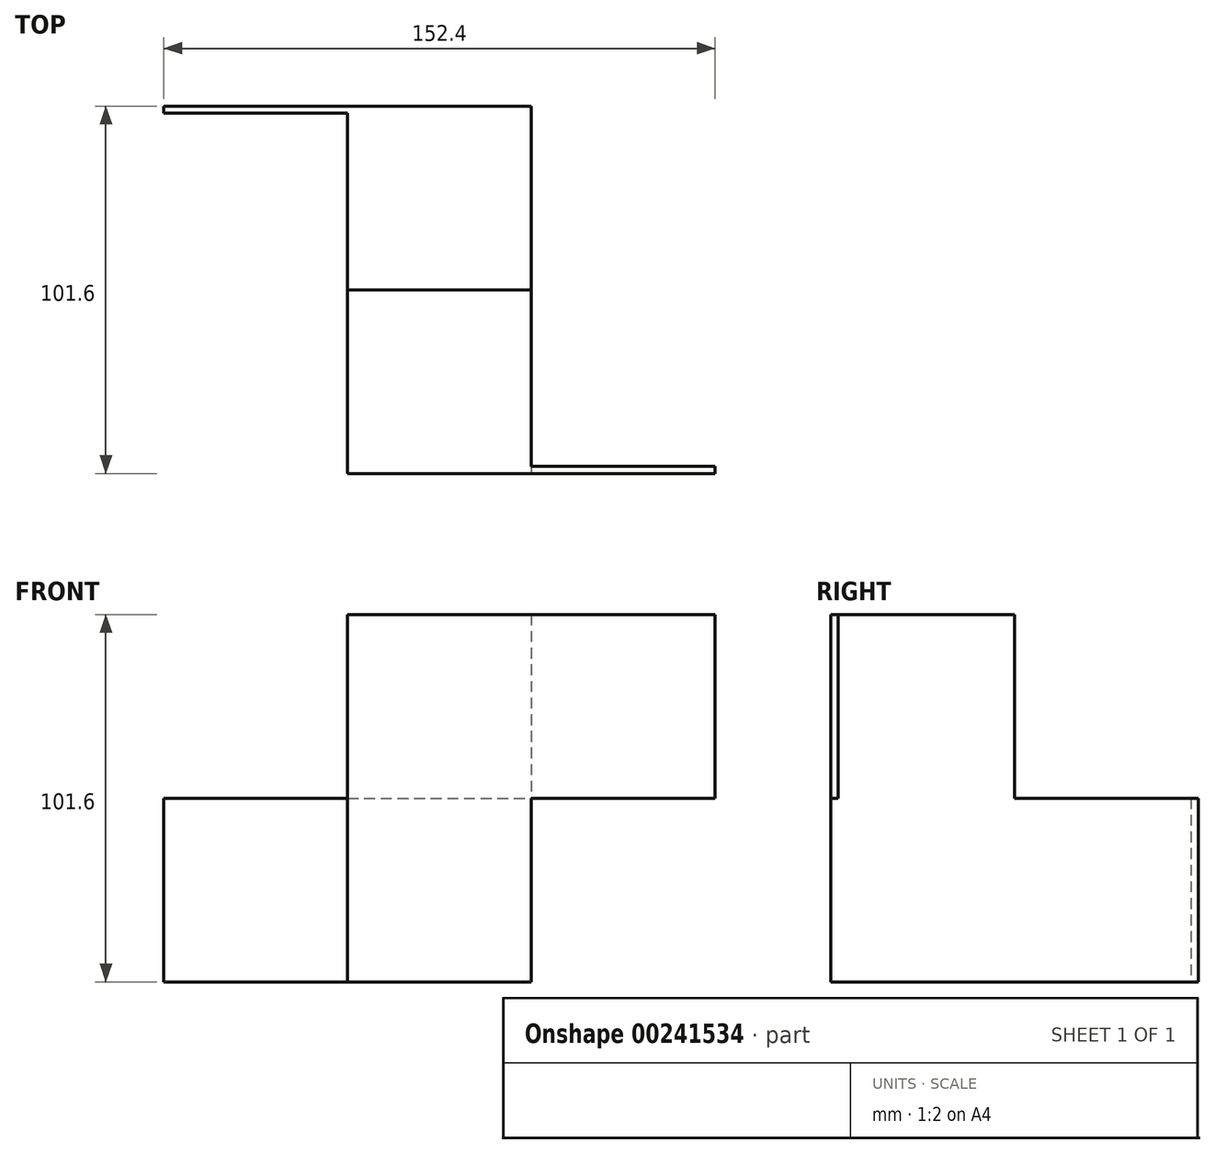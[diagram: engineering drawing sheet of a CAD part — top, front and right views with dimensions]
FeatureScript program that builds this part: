
annotation { "Feature Type Name" : "Feature", "Feature Type Description" : "" }
export const myFeature = defineFeature(function(context is Context, id is Id, definition is map)
    precondition{}
    {
        {
            assignVariable(context, id + "F0", {"name" : "B1", "anyValue" : 2});
        }
        {
            var Q0;
            Q0=qCreatedBy(makeId("Front.planeOp"),FACE);
            var sketch = newSketch(context, id + "F1", { "sketchPlane" : qUnion([Q0])});
            skLineSegment(sketch, "E0.bottom", {"start": v(-22.28, 21.96) * mm, "end": v(28.52, 21.96) * mm});
            skLineSegment(sketch, "E0.top", {"start": v(-22.28, -28.84) * mm, "end": v(28.52, -28.84) * mm});
            skLineSegment(sketch, "E0.left", {"start": v(-22.28, 21.96) * mm, "end": v(-22.28, -28.84) * mm});
            skLineSegment(sketch, "E0.right", {"start": v(28.52, 21.96) * mm, "end": v(28.52, -28.84) * mm});
            skSolve(sketch);
        }
        {
            var Q0;
            Q0=makeQuery(id+"F1.imprint","IMPRINT",FACE,{"disambiguationData":[TD([[makeQuery(id+"F1.imprint","IMPRINT",EDGE,{"derivedFrom":sQuery(id+"F1.wireOp",EDGE,"E0.bottom")}),-1.0]])]});
            extrude(context, id + "F2", {"entities" : qUnion([Q0]), "depth" : 50.8 * mm});
        }
        {
            var Q0;
            Q0=makeQuery(id+"F2.opExtrude","CAP_FACE",FACE,{"disambiguationData":[OSD([sQuery(id+"F1.wireOp",EDGE,"E0.bottom"),sQuery(id+"F1.wireOp",EDGE,"E0.top"),sQuery(id+"F1.wireOp",EDGE,"E0.left"),sQuery(id+"F1.wireOp",EDGE,"E0.right")])],"isStart":false});
            var sketch = newSketch(context, id + "F3", { "sketchPlane" : qUnion([Q0])});
            skLineSegment(sketch, "E1.bottom", {"start": v(28.52, -28.84) * mm, "end": v(79.32, -28.84) * mm});
            skLineSegment(sketch, "E1.top", {"start": v(28.52, 21.96) * mm, "end": v(79.32, 21.96) * mm});
            skLineSegment(sketch, "E1.left", {"start": v(28.52, -28.84) * mm, "end": v(28.52, 21.96) * mm});
            skLineSegment(sketch, "E1.right", {"start": v(79.32, -28.84) * mm, "end": v(79.32, 21.96) * mm});
            skSolve(sketch);
        }
        {
            var Q0;
            Q0 = qSketchRegion(id + "F3", true);
            extrude(context, id + "F4", {"entities" : qUnion([Q0]), "operationType" : NewBodyOperationType.ADD, "oppositeDirection" : true, "depth" : (getVariable(context, 'B1')) * mm});
        }
        {
            var Q0;
            Q0=makeQuery(id+"F2.opExtrude","CAP_FACE",FACE,{"disambiguationData":[OSD([sQuery(id+"F1.wireOp",EDGE,"E0.bottom"),sQuery(id+"F1.wireOp",EDGE,"E0.top"),sQuery(id+"F1.wireOp",EDGE,"E0.left"),sQuery(id+"F1.wireOp",EDGE,"E0.right")])],"isStart":false});
            var sketch = newSketch(context, id + "F5", { "sketchPlane" : qUnion([Q0])});
            skLineSegment(sketch, "E2.bottom", {"start": v(-22.28, -28.84) * mm, "end": v(28.52, -28.84) * mm});
            skLineSegment(sketch, "E2.top", {"start": v(-22.28, -79.64) * mm, "end": v(28.52, -79.64) * mm});
            skLineSegment(sketch, "E2.left", {"start": v(-22.28, -28.84) * mm, "end": v(-22.28, -79.64) * mm});
            skLineSegment(sketch, "E2.right", {"start": v(28.52, -28.84) * mm, "end": v(28.52, -79.64) * mm});
            skSolve(sketch);
        }
        {
            var Q0;
            Q0=makeQuery(id+"F5.imprint","IMPRINT",FACE,{"disambiguationData":[TD([[makeQuery(id+"F5.imprint","IMPRINT",EDGE,{"derivedFrom":sQuery(id+"F5.wireOp",EDGE,"E2.bottom")}),-1.0]])]});
            extrude(context, id + "F6", {"entities" : qUnion([Q0]), "operationType" : NewBodyOperationType.ADD, "oppositeDirection" : true, "depth" : 101.6 * mm});
        }
        {
            var Q0;
            Q0=makeQuery(id+"F6.opExtrude","CAP_FACE",FACE,{"disambiguationData":[OSD([sQuery(id+"F5.wireOp",EDGE,"E2.bottom"),sQuery(id+"F5.wireOp",EDGE,"E2.top"),sQuery(id+"F5.wireOp",EDGE,"E2.left"),sQuery(id+"F5.wireOp",EDGE,"E2.right")])],"isStart":false});
            var sketch = newSketch(context, id + "F7", { "sketchPlane" : qUnion([Q0])});
            skLineSegment(sketch, "E3.bottom", {"start": v(22.28, -79.64) * mm, "end": v(73.08, -79.64) * mm});
            skLineSegment(sketch, "E3.top", {"start": v(22.28, -28.84) * mm, "end": v(73.08, -28.84) * mm});
            skLineSegment(sketch, "E3.left", {"start": v(22.28, -79.64) * mm, "end": v(22.28, -28.84) * mm});
            skLineSegment(sketch, "E3.right", {"start": v(73.08, -79.64) * mm, "end": v(73.08, -28.84) * mm});
            skSolve(sketch);
        }
        {
            var Q0;
            Q0 = qSketchRegion(id + "F7", true);
            extrude(context, id + "F8", {"entities" : qUnion([Q0]), "operationType" : NewBodyOperationType.ADD, "oppositeDirection" : true, "depth" : (getVariable(context, 'B1')) * mm});
        }
    });
